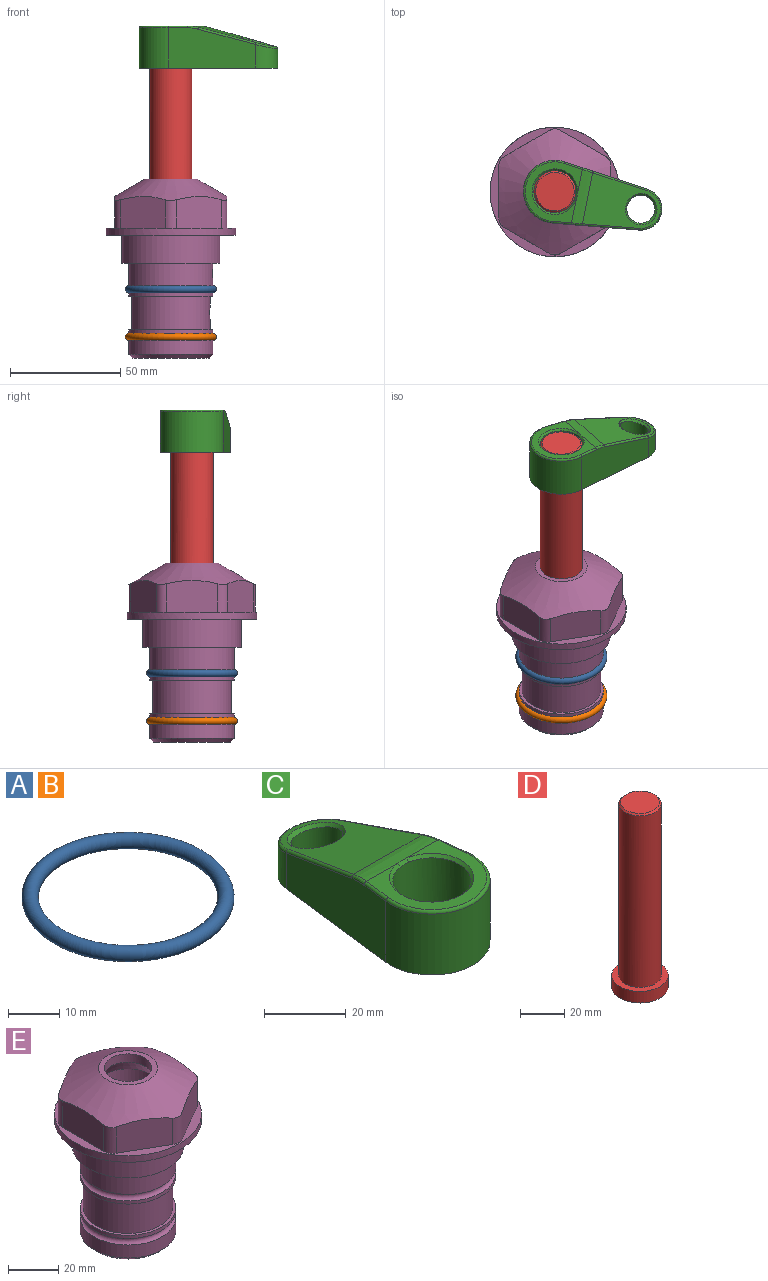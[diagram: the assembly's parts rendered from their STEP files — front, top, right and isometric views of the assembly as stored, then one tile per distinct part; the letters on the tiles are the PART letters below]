
ASSEMBLY  parts=5 mates=4
PART A: 1 faces, bbox 44.7x44.7x3.2 mm
  f0: torus R=19.05mm, axis (0,0,1), area 1193.9mm2
PART B: same geometry as A
PART C: 31 faces, bbox 31.7x65.5x19.8 mm
  f0: plane 39.12x18.26mm, normal (0.99,0.12,0), area 612.2mm2, adj f1,f4,f7,f11,f13,f15
  f1: cylinder r=9.53mm len=18.91mm, axis (0,0,-1), area 296.1mm2, adj f0,f2,f7,f17
  f2: plane 39.12x18.26mm, normal (-0.99,0.12,0), area 612.2mm2, adj f1,f4,f7,f12,f14,f16
  f3: cylinder r=6.35mm len=12.7mm, axis (0,0,-1), area 362.4mm2, adj f7,f18
  f4: cylinder r=14.29mm len=28.58mm, axis (0,0,-1), area 882.2mm2, adj f0,f2,f7,f10
  f5: cylinder r=9.53mm len=19.05mm, axis (0,0,-1), area 1092.6mm2, adj f7,f19,f20
  f6: plane 26.99x23.69mm, normal (0,0,1), area 216.2mm2, adj f9,f10,f11,f12,f19
  f7: plane 63.5x28.58mm, normal (0,0,-1), area 661.8mm2, adj f0,f1,f2,f3,f4,f5,f22,f23
  f8: plane 33.52x23.6mm, normal (0,0.26,0.97), area 486mm2, adj f9,f15,f16,f17,f18
  f9: cylinder r=19.05mm len=24.72mm, axis (1,0,0), area 120.4mm2, adj f6,f8,f13,f14,f20
  f10: torus R=13.49mm, axis (0,0,1), area 59mm2, adj f4,f6,f11,f12
  f11: cylinder r=0.79mm len=8.67mm, axis (0.12,-0.99,0), area 10.8mm2, adj f0,f6,f10,f13
  f12: cylinder r=0.79mm len=8.67mm, axis (0.12,0.99,0), area 10.8mm2, adj f2,f6,f10,f14
  f13: bspline ~4.95x1.42mm, area 6.1mm2, adj f0,f9,f11,f15
  f14: bspline ~4.95x1.42mm, area 6.1mm2, adj f2,f9,f12,f16
  f15: cylinder r=0.79mm len=25.95mm, axis (0.12,-0.96,0.26), area 32.9mm2, adj f0,f8,f13,f17
  f16: cylinder r=0.79mm len=25.95mm, axis (0.12,0.96,-0.26), area 32.9mm2, adj f2,f8,f14,f17
  f17: bspline ~18.91x8.38mm, area 30mm2, adj f1,f8,f15,f16
  f18: bspline ~14.29x14.29mm, area 48.3mm2, adj f3,f8
  f19: cone r=9.53mm half-angle=45deg, axis (0,0,1), area 66.5mm2, adj f5,f6,f20
  f20: bspline ~3.22x0.96mm, area 3.5mm2, adj f5,f9,f19
  f21: plane 2.75x2.72mm, normal (0,0,-1), area 2.9mm2, adj f23,f25,f28
  f22: plane 23.05x15.88mm, normal (-0.99,-0.12,0), area 323.6mm2, adj f7,f25,f26,f27,f28,f29
  f23: plane 23.05x15.88mm, normal (0.99,-0.12,0), area 323.6mm2, adj f7,f21,f25,f27,f28,f30
  f24: cylinder r=9.53mm len=10.69mm, axis (0,0,-1), area 114.7mm2, adj f7,f27,f29,f30
  f25: cylinder r=12.7mm len=20.59mm, axis (0,0,-1), area 381.1mm2, adj f7,f21,f22,f23,f26,f28
  f26: plane 2.75x2.72mm, normal (0,0,-1), area 2.9mm2, adj f22,f25,f28
  f27: plane 19.72x18.37mm, normal (0,-0.26,-0.97), area 291.8mm2, adj f22,f23,f24,f28,f29,f30
  f28: cylinder r=15.88mm len=19.92mm, axis (1,0,0), area 54.8mm2, adj f21,f22,f23,f25,f26,f27
  f29: cylinder r=1.59mm len=11mm, axis (0,0,-1), area 34.7mm2, adj f7,f22,f24,f27
  f30: cylinder r=1.59mm len=11mm, axis (0,0,-1), area 34.7mm2, adj f7,f23,f24,f27
PART D: 6 faces, bbox 25.4x25.4x101.6 mm
  f0: plane 17.46x17.46mm, normal (0,0,1), area 239.5mm2, adj f5
  f1: plane 25.4x25.4mm, normal (0,0,-1), area 506.7mm2, adj f2
  f2: cylinder r=12.7mm len=25.4mm, axis (0,0,1), area 506.7mm2, adj f1,f3
  f3: plane 25.4x25.4mm, normal (0,0,1), area 221.7mm2, adj f2,f4
  f4: cylinder r=9.53mm len=94.46mm, axis (0,0,1), area 5653mm2, adj f3,f5
  f5: cone r=8.73mm half-angle=45deg, axis (0,0,-1), area 64.4mm2, adj f0,f4
PART E: 36 faces, bbox 58.7x58.7x81 mm
  f0: cylinder r=17.78mm len=35.56mm, axis (0,0,1), area 1670.8mm2, adj f23,f24,f31
  f1: cylinder r=19.05mm len=38.1mm, axis (0,0,1), area 1191.9mm2, adj f26,f27,f30
  f2: plane 58.66x58.66mm, normal (0,0,-1), area 1150.6mm2, adj f3,f28
  f3: cylinder r=29.33mm len=58.66mm, axis (0,0,-1), area 585.1mm2, adj f2,f4
  f4: plane 58.66x58.66mm, normal (0,0,1), area 475.9mm2, adj f3,f5,f6,f7,f8,f9,f10,f11
  f5: plane 20.32x14.34mm, normal (-0.5,0.87,0), area 324.4mm2, adj f4,f15,f16,f17
  f6: plane 20.32x14.34mm, normal (0.5,0.87,0), area 324.4mm2, adj f4,f14,f15,f17
  f7: plane 23.48x14.34mm, normal (1,0,0), area 324.4mm2, adj f4,f13,f14,f17
  f8: plane 20.32x14.34mm, normal (0.5,-0.87,0), area 324.4mm2, adj f4,f12,f13,f17
  f9: plane 20.32x14.34mm, normal (-0.5,-0.87,0), area 324.4mm2, adj f4,f11,f12,f17
  f10: plane 23.48x14.34mm, normal (-1,0,0), area 324.4mm2, adj f4,f11,f16,f17
  f11: cylinder r=5.08mm len=12.85mm, axis (0,0,-1), area 67.2mm2, adj f4,f9,f10,f17
  f12: cylinder r=5.08mm len=12.85mm, axis (0,0,-1), area 67.2mm2, adj f4,f8,f9,f17
  f13: cylinder r=5.08mm len=12.85mm, axis (0,0,-1), area 67.2mm2, adj f4,f7,f8,f17
  f14: cylinder r=5.08mm len=12.85mm, axis (0,0,-1), area 67.2mm2, adj f4,f6,f7,f17
  f15: cylinder r=5.08mm len=12.85mm, axis (0,0,-1), area 67.2mm2, adj f4,f5,f6,f17
  f16: cylinder r=5.08mm len=12.85mm, axis (0,0,-1), area 67.2mm2, adj f4,f5,f10,f17
  f17: cone r=11.73mm half-angle=60deg, axis (0,0,-1), area 2071.8mm2, adj f5,f6,f7,f8,f9,f10,f11,f12
  f18: plane 23.46x23.46mm, normal (0,0,1), area 147.4mm2, adj f17,f35
  f19: plane 34.93x34.93mm, normal (0,0,-1), area 958mm2, adj f29
  f20: cylinder r=19.05mm len=38.1mm, axis (0,0,1), area 760.1mm2, adj f21,f29
  f21: torus R=19.05mm, axis (0,0,1), area 565.3mm2, adj f20,f22
  f22: cylinder r=19.05mm len=38.1mm, axis (0,0,1), area 190mm2, adj f21,f23
  f23: plane 38.1x38.1mm, normal (0,0,1), area 146.9mm2, adj f0,f22
  f24: plane 38.1x38.1mm, normal (0,0,-1), area 146.9mm2, adj f0,f25
  f25: cylinder r=19.05mm len=38.1mm, axis (0,0,1), area 190mm2, adj f24,f26
  f26: torus R=19.05mm, axis (0,0,1), area 565.3mm2, adj f1,f25
  f27: plane 44.45x44.45mm, normal (0,0,-1), area 411.7mm2, adj f1,f28
  f28: cylinder r=22.23mm len=44.45mm, axis (0,0,1), area 1773.5mm2, adj f2,f27
  f29: cone r=19.05mm half-angle=45deg, axis (0,0,1), area 257.5mm2, adj f19,f20
  f30: cylinder r=3.17mm len=6.75mm, axis (-1,0,0), area 128mm2, adj f1,f33
  f31: cylinder r=3.17mm len=6.35mm, axis (-1,0,0), area 102.5mm2, adj f0,f33
  f32: plane 25.4x25.4mm, normal (0,0,1), area 506.7mm2, adj f33
  f33: cylinder r=12.7mm len=66.42mm, axis (0,0,-1), area 5236.2mm2, adj f30,f31,f32,f34
  f34: cone r=9.53mm half-angle=30deg, axis (0,0,-1), area 443.4mm2, adj f33,f35
  f35: cylinder r=9.53mm len=19.05mm, axis (0,0,-1), area 240.9mm2, adj f18,f34
PLACE A at identity
PLACE B t=(0,0,-21.59)mm
PLACE C rot(axis=(0,0,-1),101.5deg) t=(0,0,31.21)mm
PLACE D rot(axis=(0,0,-1),101.5deg) t=(0,0,30.41)mm
PLACE E at identity fixed
MATE fastened B.f0 <-> E.f0  axis (0,0,1) through (0,0,-46.1)mm
MATE fastened D.f2 <-> C.f4  axis (0,0,1) through (0,0,93.91)mm
MATE cylindrical D.f2 <-> E.f0  axis (0,0,-1) through (0,0,-7.69)mm
MATE fastened A.f0 <-> E.f0  axis (0,0,1) through (0,0,-24.51)mm
